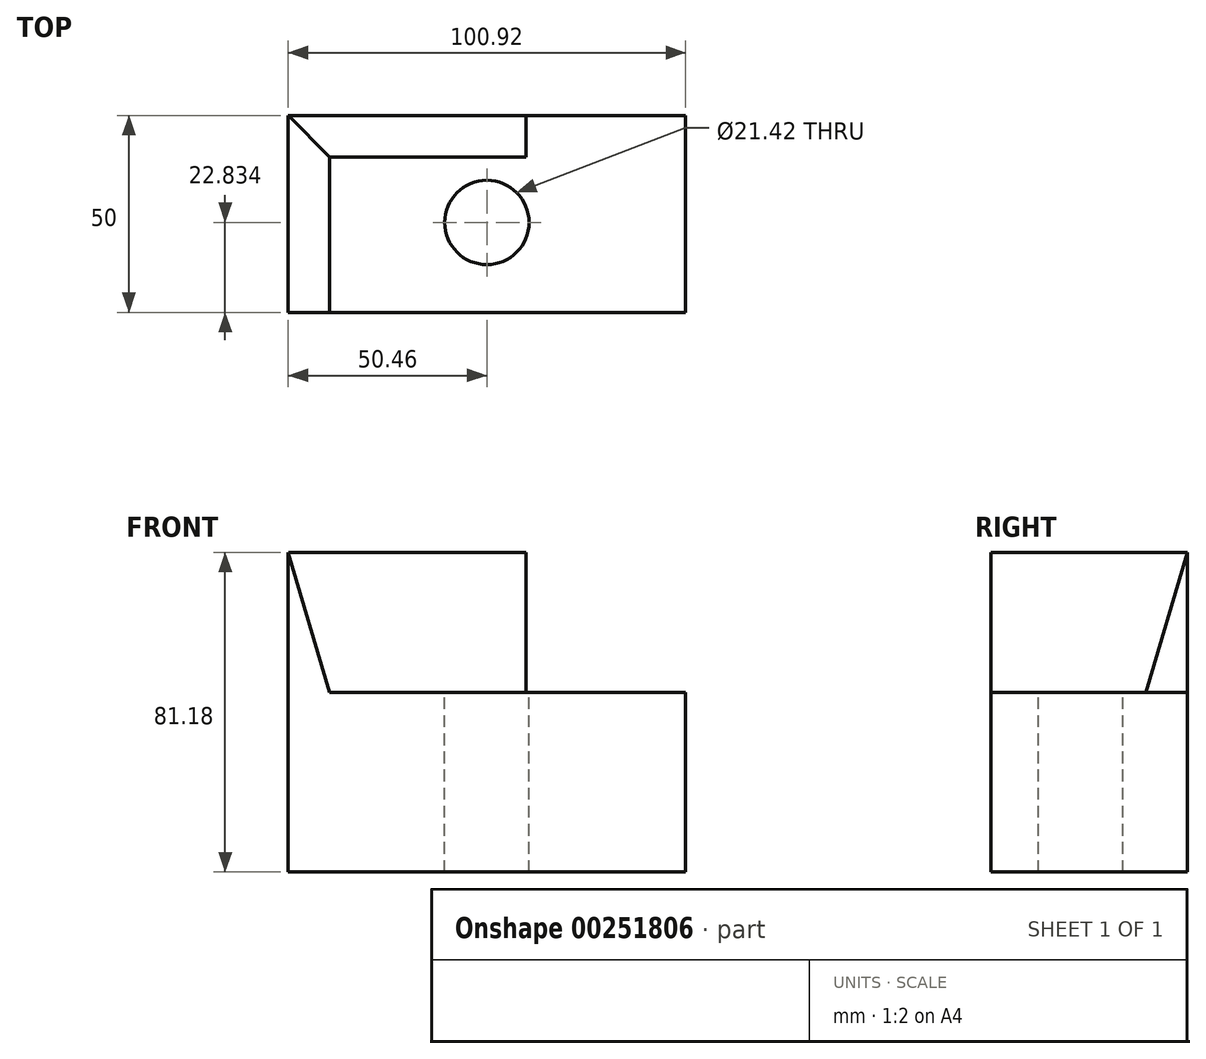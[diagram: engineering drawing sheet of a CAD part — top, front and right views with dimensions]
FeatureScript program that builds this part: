
annotation { "Feature Type Name" : "Feature", "Feature Type Description" : "" }
export const myFeature = defineFeature(function(context is Context, id is Id, definition is map)
    precondition{}
    {
        {
            var Q0;
            Q0=qCreatedBy(makeId("Front.planeOp"),FACE);
            var sketch = newSketch(context, id + "F0", { "sketchPlane" : qUnion([Q0])});
            skLineSegment(sketch, "E0.bottom", {"start": v(-50.46, 22.82) * mm, "end": v(50.46, 22.82) * mm});
            skLineSegment(sketch, "E0.top", {"start": v(-50.46, -22.82) * mm, "end": v(50.46, -22.82) * mm});
            skLineSegment(sketch, "E0.left", {"start": v(-50.46, 22.82) * mm, "end": v(-50.46, -22.82) * mm});
            skLineSegment(sketch, "E0.right", {"start": v(50.46, 22.82) * mm, "end": v(50.46, -22.82) * mm});
            skPoint(sketch, "E0.middle", {"position": v(0, 0) * mm});
            skLineSegment(sketch, "E1", {"start": v(-50.46, 22.82) * mm, "end": v(-50.46, 58.36) * mm});
            skLineSegment(sketch, "E2", {"start": v(-50.46, 58.36) * mm, "end": v(-39.93, 22.82) * mm});
            skSolve(sketch);
        }
        {
            var Q0;
            {var subQ0=sQuery(id+"F0.wireOp",EDGE,"E1");Q0=makeQuery(id+"F0.imprint","IMPRINT",FACE,{"disambiguationData":[TD([[makeQuery(id+"F0.imprint","IMPRINT",EDGE,{"derivedFrom":subQ0}),-1.0]])]});}
            var Q1;
            Q1=makeQuery(id+"F0.imprint","IMPRINT",FACE,{"disambiguationData":[TD([[makeQuery(id+"F0.imprint","IMPRINT",EDGE,{"derivedFrom":sQuery(id+"F0.wireOp",EDGE,"E0.top")}),1.0]])]});
            extrude(context, id + "F1", {"entities" : qUnion([Q0, Q1]), "oppositeDirection" : true, "depth" : 50 * mm});
        }
        {
            var Q0;
            Q0=qCreatedBy(makeId("Right.planeOp"),FACE);
            var sketch = newSketch(context, id + "F2", { "sketchPlane" : qUnion([Q0])});
            skLineSegment(sketch, "E3", {"start": v(50, 22.82) * mm, "end": v(50, 58.36) * mm});
            skLineSegment(sketch, "E4", {"start": v(50, 58.36) * mm, "end": v(39.46, 22.82) * mm});
            skLineSegment(sketch, "E5", {"start": v(39.46, 22.82) * mm, "end": v(50, 22.82) * mm});
            skSolve(sketch);
        }
        {
            var Q0;
            Q0=makeQuery(id+"F2.imprint","IMPRINT",FACE,{"disambiguationData":[TD([[makeQuery(id+"F2.imprint","IMPRINT",EDGE,{"derivedFrom":sQuery(id+"F2.wireOp",EDGE,"E3")}),1.0]])]});
            extrude(context, id + "F3", {"entities" : qUnion([Q0]), "operationType" : NewBodyOperationType.ADD, "oppositeDirection" : true, "depth" : 50.4 * mm});
        }
        {
            var Q0;
            Q0=makeQuery(id+"F1.opExtrude","SWEPT_FACE",FACE,{"disambiguationData":[OSD([sQuery(id+"F0.wireOp",EDGE,"E0.bottom")])]});
            var sketch = newSketch(context, id + "F4", { "sketchPlane" : qUnion([Q0])});
            skCircle(sketch, "E6", {"center": v(0, 22.83) * mm, "radius": 10.71 * mm});
            skSolve(sketch);
        }
        {
            var Q0;
            Q0=makeQuery(id+"F4.imprint","IMPRINT",FACE,{"disambiguationData":[TD([[makeQuery(id+"F4.imprint","IMPRINT",EDGE,{"derivedFrom":sQuery(id+"F4.wireOp",EDGE,"E6")}),1.0]])]});
            extrude(context, id + "F5", {"entities" : qUnion([Q0]), "operationType" : NewBodyOperationType.REMOVE, "oppositeDirection" : true, "depth" : 50 * mm});
        }
        {
            var Q0;
            Q0=makeQuery(id+"F3.opExtrude","CAP_FACE",FACE,{"disambiguationData":[OSD([sQuery(id+"F2.wireOp",EDGE,"E3"),sQuery(id+"F2.wireOp",EDGE,"E4"),sQuery(id+"F2.wireOp",EDGE,"E5")])],"isStart":true});
            extrude(context, id + "F6", {"entities" : qUnion([Q0]), "operationType" : NewBodyOperationType.ADD, "depth" : 10 * mm});
        }
    });
